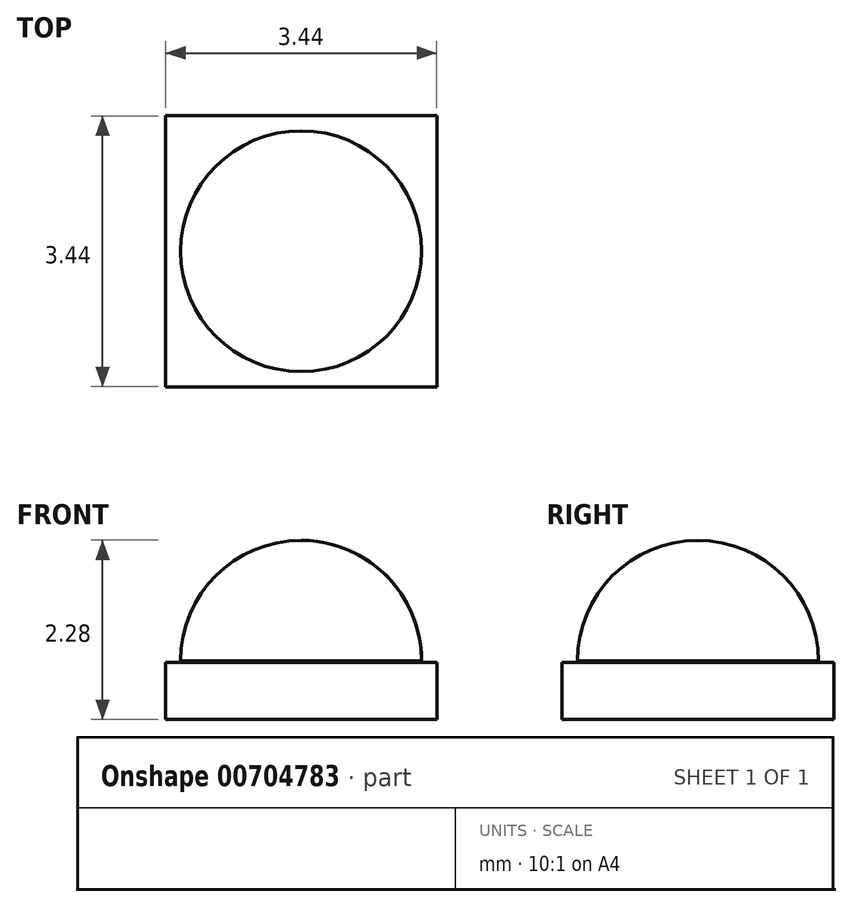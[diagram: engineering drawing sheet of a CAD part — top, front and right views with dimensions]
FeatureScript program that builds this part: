
annotation { "Feature Type Name" : "Feature", "Feature Type Description" : "" }
export const myFeature = defineFeature(function(context is Context, id is Id, definition is map)
    precondition{}
    {
        {
            var Q0;
            Q0=qCreatedBy(makeId("Top.planeOp"),FACE);
            var sketch = newSketch(context, id + "F0", { "sketchPlane" : qUnion([Q0])});
            skLineSegment(sketch, "E0.bottom", {"start": v(1.72, -1.73) * mm, "end": v(-1.72, -1.73) * mm});
            skLineSegment(sketch, "E0.top", {"start": v(1.73, 1.73) * mm, "end": v(-1.72, 1.73) * mm});
            skLineSegment(sketch, "E0.left", {"start": v(1.73, -1.73) * mm, "end": v(1.73, 1.73) * mm});
            skLineSegment(sketch, "E0.right", {"start": v(-1.72, -1.73) * mm, "end": v(-1.72, 1.72) * mm});
            skPoint(sketch, "E0.middle", {"position": v(0, 0) * mm});
            skSolve(sketch);
        }
        {
            var Q0;
            Q0 = qSketchRegion(id + "F0", true);
            extrude(context, id + "F1", {"entities" : qUnion([Q0]), "depth" : .73 * mm, "offsetDistance" : 25 * mm});
        }
        {
            var Q0;
            Q0=makeQuery(id+"F1.opExtrude","CAP_FACE",FACE,{"disambiguationData":[OSD([sQuery(id+"F0.wireOp",EDGE,"E0.bottom"),sQuery(id+"F0.wireOp",EDGE,"E0.top"),sQuery(id+"F0.wireOp",EDGE,"E0.left"),sQuery(id+"F0.wireOp",EDGE,"E0.right")])],"isStart":false});
            var sketch = newSketch(context, id + "F2", { "sketchPlane" : qUnion([Q0])});
            skPoint(sketch, "E1", {"position": v(0, 0) * mm});
            skCircle(sketch, "E2", {"center": v(0, 0) * mm, "radius": 1.53 * mm});
            skSolve(sketch);
        }
        {
            var Q0;
            Q0=qCreatedBy(makeId("Front.planeOp"),FACE);
            var sketch = newSketch(context, id + "F3", { "sketchPlane" : qUnion([Q0])});
            skLineSegment(sketch, "E3", {"start": v(0, 0) * mm, "end": v(0, 2.26) * mm});
            skLineSegment(sketch, "E4", {"start": v(0, 0.75) * mm, "end": v(1.53, 0.75) * mm});
            skArc(sketch, "E5", {"start": v(1.53, 0.75) * mm, "mid": v(1.08, 1.83) * mm, "end": v(0, 2.28) * mm});
            skLineSegment(sketch, "E6", {"start": v(0, 0.75) * mm, "end": v(0, 2.28) * mm});
            skSolve(sketch);
        }
        {
            var Q0;
            {var subQ0=sQuery(id+"F3.wireOp",EDGE,"E4");Q0=makeQuery(id+"F3.imprint","IMPRINT",FACE,{"disambiguationData":[TD([[makeQuery(id+"F3.imprint","IMPRINT",EDGE,{"derivedFrom":subQ0}),1.0]])]});}
            var Q1;
            Q1=sQuery(id+"F2.wireOp",EDGE,"E2");
            revolve(context, id + "F4", {"surfaceOperationType" : NewSurfaceOperationType.NEW, "entities" : qUnion([Q0]), "axis" : qUnion([Q1]), "revolveType" : RevolveType.FULL});
        }
    });
